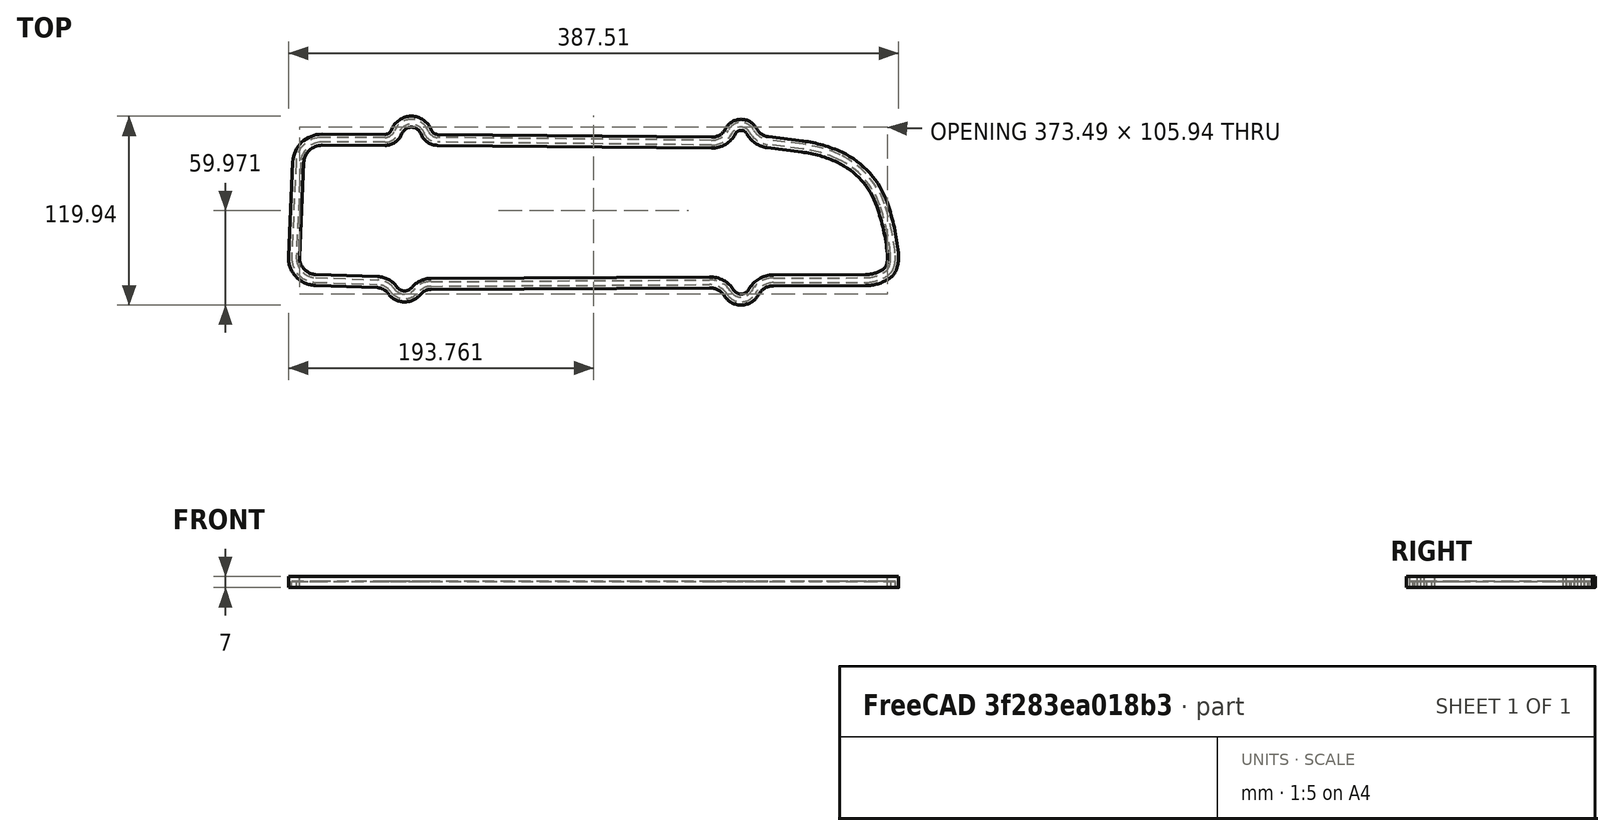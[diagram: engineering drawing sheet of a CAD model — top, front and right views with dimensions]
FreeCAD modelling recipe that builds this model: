
FCSTD DOCUMENT  (FreeCAD 1.1R40971 (Git))
Label: TailLightHousing
License: All rights reserved
LicenseURL: http://en.wikipedia.org/wiki/All_rights_reserved
objects: Sketcher::SketchObject×2, Mesh::Feature×1, PartDesign::Plane×1, App::Point×1, PartDesign::AdditivePipe×1, PartDesign::Body×1
note: 9 computed .brp shape members not serialized (recipe doc carries the construction recipe); baked Part::Feature solids carry a one-line shape summary decoded from their .brp

FEATURE [Mesh::Feature] MeshingTaillightAligned
FEATURE [Sketcher::SketchObject] Sketch  label="GasketPath"
  ArcFitTolerance = 1e-06
  AttachmentSupport = -> [XY_Plane]
  ExternalTypes = [0]
  FullyConstrained = true
  MakeInternals = false
  MapMode = 5
  sketch-geometry (27):
    g0: LineSegment StartX=-100 StartY=-72 StartZ=0 EndX=77 EndY=-71 EndZ=0
    g1: LineSegment StartX=117.5 StartY=-69.75 StartZ=0 EndX=176.08 EndY=-69.5756 EndZ=0
    g2: LineSegment StartX=78.1945 StartY=17.6877 StartZ=0 EndX=-95.75 EndY=19.5 EndZ=0
    g3: LineSegment StartX=-129.25 StartY=19.5 StartZ=0 EndX=-169.243 EndY=19.5618 EndZ=0
    g4: LineSegment StartX=-184.25 StartY=5.25 StartZ=0 EndX=-187 EndY=-54.6239 EndZ=0
    g5: LineSegment StartX=-173.262 StartY=-69.5191 StartZ=0 EndX=-134 EndY=-70.89 EndZ=0
    g6: ArcOfCircle CenterX=-134.428 CenterY=-83.1489 CenterZ=0 NormalX=0 NormalY=0 NormalZ=1 AngleXU=0 Radius=12.2664 StartAngle=0.622932 EndAngle=1.53589
    g7: ArcOfCircle CenterX=-116.75 CenterY=-70.45 CenterZ=0 NormalX=0 NormalY=0 NormalZ=1 AngleXU=0 Radius=9.5 StartAngle=3.76452 EndAngle=5.5955
    g8: ArcOfCircle CenterX=-99.9307 CenterY=-84.2662 CenterZ=0 NormalX=0 NormalY=0 NormalZ=1 AngleXU=0 Radius=12.2664 StartAngle=1.57645 EndAngle=2.45391
    g9: ArcOfCircle CenterX=-172.765 CenterY=-55.2777 CenterZ=0 NormalX=0 NormalY=0 NormalZ=1 AngleXU=0 Radius=14.25 StartAngle=3.0957 EndAngle=4.67749
    g10: ArcOfCircle CenterX=-169.266 CenterY=4.56178 CenterZ=0 NormalX=0 NormalY=0 NormalZ=1 AngleXU=0 Radius=15 StartAngle=1.56925 EndAngle=3.0957
    g11: ArcOfCircle CenterX=-129.238 CenterY=27.5 CenterZ=0 NormalX=0 NormalY=0 NormalZ=1 AngleXU=0 Radius=8 StartAngle=4.71084 EndAngle=5.91373
    g12: ArcOfCircle CenterX=-112.452 CenterY=21 CenterZ=0 NormalX=0 NormalY=0 NormalZ=1 AngleXU=0 Radius=10 StartAngle=0.369433 EndAngle=2.77213
    g13: ArcOfCircle CenterX=-95.6667 CenterY=27.4996 CenterZ=0 NormalX=0 NormalY=0 NormalZ=1 AngleXU=0 Radius=8 StartAngle=3.51103 EndAngle=4.70197
    g14: ArcOfCircle CenterX=77.0819 CenterY=-85.4998 CenterZ=0 NormalX=0 NormalY=0 NormalZ=1 AngleXU=0 Radius=14.5 StartAngle=0.563877 EndAngle=1.57645
    g15: ArcOfCircle CenterX=96.9439 CenterY=-72.9398 CenterZ=0 NormalX=0 NormalY=0 NormalZ=1 AngleXU=0 Radius=9 StartAngle=3.70547 EndAngle=5.78107
    g16: ArcOfCircle CenterX=117.543 CenterY=-84.2499 CenterZ=0 NormalX=0 NormalY=0 NormalZ=1 AngleXU=0 Radius=14.5 StartAngle=1.57377 EndAngle=2.63948
    g17: ArcOfCircle CenterX=78.3352 CenterY=31.187 CenterZ=0 NormalX=0 NormalY=0 NormalZ=1 AngleXU=0 Radius=13.5 StartAngle=4.70197 EndAngle=5.80711
    g18: ArcOfCircle CenterX=97 CenterY=21.5628 CenterZ=0 NormalX=0 NormalY=0 NormalZ=1 AngleXU=0 Radius=7.5 StartAngle=0.494276 EndAngle=2.66552
    g19: ArcOfCircle CenterX=115.707 CenterY=31.6437 CenterZ=0 NormalX=0 NormalY=0 NormalZ=1 AngleXU=0 Radius=13.75 StartAngle=3.63587 EndAngle=4.58795
    g20: LineSegment StartX=114 StartY=18 StartZ=0 EndX=136 EndY=15.2481 EndZ=0
    g21: ArcOfCircle CenterX=126.319 CenterY=-62.1488 CenterZ=0 NormalX=0 NormalY=0 NormalZ=1 AngleXU=0 Radius=78 StartAngle=1.13139 EndAngle=1.44636
    g22: ArcOfCircle CenterX=137.379 CenterY=-38.6186 CenterZ=0 NormalX=0 NormalY=0 NormalZ=1 AngleXU=0 Radius=52 StartAngle=0.329603 EndAngle=1.13139
    g23: ArcOfCircle CenterX=176.009 CenterY=-45.5757 CenterZ=0 NormalX=0 NormalY=0 NormalZ=1 AngleXU=0 Radius=24 StartAngle=4.71537 EndAngle=5.28835
    g24: ArcOfCircle CenterX=184.451 CenterY=-58.5751 CenterZ=0 NormalX=0 NormalY=0 NormalZ=1 AngleXU=0 Radius=8.5 StartAngle=5.28835 EndAngle=5.99521
    g25: ArcOfCircle CenterX=171.986 CenterY=-54.8829 CenterZ=0 NormalX=0 NormalY=0 NormalZ=1 AngleXU=0 Radius=21.5 StartAngle=5.99521 EndAngle=6.38658
    g26: ArcOfCircle CenterX=54.0655 CenterY=-67.1187 CenterZ=0 NormalX=0 NormalY=0 NormalZ=1 AngleXU=0 Radius=140.053 StartAngle=0.103393 EndAngle=0.329603
  constraints (74):
    c: Tangent(g6,g5) = 1.5708
    c: Tangent(g8,g0) = 1.5708
    c: Tangent(g8,g7) = 1.5708
    c: Tangent(g7,g6) = 1.5708
    c: Equal(g6,g8)
    c: DistanceX(g0,g-1) = 100
    c: DistanceY(g0,g-1) = 72
    c: DistanceY(g0,g-1) = 71
    c: Radius(g7) = 9.5
    c: DistanceX(g7,g0) = 16.75
    c: DistanceY(g0,g7) = 1.55
    c: DistanceX(g5,g0) = 34
    c: DistanceY(g0,g5) = 1.11
    c: Tangent(g9,g5) = -1.5708
    c: Tangent(g9,g4) = -1.5708
    c: Radius(g9) = 14.25
    c: DistanceX(g4,g0) = 87
    c: Tangent(g10,g3) = -1.5708
    c: Tangent(g10,g4) = -1.5708
    c: Radius(g10) = 15
    c: DistanceX(g4,g0) = 84.25
    c: DistanceY(g0,g4) = 77.25
    c: Tangent(g11,g3) = 1.5708
    c: Tangent(g12,g11) = 1.5708
    c: Tangent(g13,g12) = 1.5708
    c: Tangent(g13,g2) = 1.5708
    c: Radius(g11) = 8
    c: Radius(g13) = 8
    c: Radius(g12) = 10
    c: DistanceY(g0,g3) = 91.5
    c: DistanceX(g3,g0) = 29.25
    c: DistanceY(g0,g12) = 93
    c: DistanceY(g0,g2) = 91.5
    c: DistanceX(g0,g2) = 4.25
    c: Tangent(g16,g1) = 1.5708
    c: Tangent(g16,g15) = 1.5708
    c: Tangent(g15,g14) = 1.5708
    c: Tangent(g14,g0) = 1.5708
    c: Radius(g15) = 9
    c: Radius(g14) = 14.5
    c: DistanceX(g0,g0) = 177
    c: DistanceY(g14,g0) = 6.75
    c: Radius(g16) = 14.5
    c: DistanceX(g0,g1) = 40.5
    c: DistanceY(g0,g1) = 1.25
    c: Tangent(g20,g19) = -1.5708
    c: Tangent(g19,g18) = 1.5708
    c: Tangent(g18,g17) = 1.5708
    c: Tangent(g17,g2) = 1.5708
    c: Radius(g17) = 13.5
    c: Radius(g18) = 7.5
    c: Radius(g19) = 13.75
    c: DistanceY(g0,g19) = 89
    c: DistanceX(g0,g19) = 37
    c: DistanceX(g0,g18) = 20
    c: DistanceY(g0,g17) = 96
    c: Tangent(g21,g20) = 1.5708
    c: Radius(g21) = 78
    c: Tangent(g22,g21) = -1.5708
    c: Radius(g22) = 52
    c: Tangent(g23,g1) = -1.5708
    c: Radius(g23) = 24
    c: Tangent(g24,g23) = -1.5708
    c: Tangent(g25,g24) = -1.5708
    c: Radius(g24) = 8.5
    c: Radius(g25) = 21.5
    c: Angle(g24) = 0.706858
    c: Tangent(g26,g22) = -1.5708
    c: Tangent(g26,g25) = -1.5708
    c: DistanceX(g1,g23) = 13
    c: DistanceX(g20,g21) = 23.5
    c: DistanceX(g1,g22) = 10.5
    c: DistanceX(g19,g20) = 22
    c: DistanceX(g1,g1) = 58.58
FEATURE [PartDesign::Plane] DatumPlane
  AttachmentSupport = -> [Sketch]
  Length = 110.473
  MapMode = 7
  Placement = pos=(-100,-72,0) rot=(0.579525,-0.57626,-0.57626;2.09114rad)
  ResizeMode = 0
  Width = 63.8978
FEATURE [Sketcher::SketchObject] Sketch001
  ArcFitTolerance = 1e-06
  AttachmentSupport = -> [DatumPlane]
  ExternalTypes = [0]
  FullyConstrained = true
  MakeInternals = false
  MapMode = 5
  Placement = pos=(-100,-72,0) rot=(0.579525,-0.57626,-0.57626;2.09114rad)
  sketch-geometry (8):
    g0: LineSegment StartX=-3.5 StartY=0 StartZ=0 EndX=3.5 EndY=0 EndZ=0
    g1: LineSegment StartX=3.5 StartY=0 StartZ=0 EndX=3.5 EndY=-7 EndZ=0
    g2: LineSegment StartX=-3.5 StartY=-7 StartZ=0 EndX=-3.5 EndY=0 EndZ=0
    g3: LineSegment StartX=-3.5 StartY=-7 StartZ=0 EndX=-1.5 EndY=-7 EndZ=0
    g4: LineSegment StartX=-1.5 StartY=-7 StartZ=0 EndX=-1.5 EndY=-3 EndZ=0
    g5: LineSegment StartX=-1.5 StartY=-3 StartZ=0 EndX=1.5 EndY=-3 EndZ=0
    g6: LineSegment StartX=1.5 StartY=-3 StartZ=0 EndX=1.5 EndY=-7 EndZ=0
    g7: LineSegment StartX=1.5 StartY=-7 StartZ=0 EndX=3.5 EndY=-7 EndZ=0
  constraints (23):
    c: Coincident(g0,g1)
    c: Coincident(g2,g0)
    c: Horizontal(g0)
    c: Vertical(g1)
    c: Vertical(g2)
    c: DistanceY(g1,g1) = -7
    c: Distance(g1,g2) = 7
    c: Symmetric(g0,g0,g-1)
    c: Coincident(g3,g2)
    c: Horizontal(g3)
    c: Coincident(g4,g3)
    c: Vertical(g4)
    c: Coincident(g5,g4)
    c: Horizontal(g5)
    c: Coincident(g6,g5)
    c: Vertical(g6)
    c: Coincident(g7,g6)
    c: Coincident(g7,g1)
    c: Horizontal(g7)
    c: Equal(g3,g7)
    c: DistanceY(g4,g4) = -4
    c: Horizontal(g3,g6)
    c: Distance(g5,g5) = 3
FEATURE [App::Point] Origin001  label="Origin"
  Role = Origin
FEATURE [PartDesign::AdditivePipe] AdditivePipe
  AuxilleryCurvelinear = true
  AuxillerySpineTangent = false
  Binormal = (0,0,0)
  Mode = 0
  Placement = pos=(-100,-72,0) rot=(0.579525,-0.57626,-0.57626;2.09114rad)
  Profile = -> Sketch001
  Refine = true
  Spine = -> Sketch [Edge3,Edge4,Edge5,Edge6,Edge7,Edge8,Edge9,Edge10,Edge11,Edge12,Edge13,Edge14,Edge15,Edge16,Edge17,Edge18,Edge19,Edge20,Edge21,Edge22,Edge23,Edge24,Edge25,Edge26,Edge27,Edge1,Edge2]
  SpineTangent = false
  Suppressed = false
  Transformation = 0
  Transition = 0
FEATURE [PartDesign::Body] Body
  AllowCompound = false
  Group = -> [Sketch,DatumPlane,Sketch001,AdditivePipe]
  Origin = -> Origin
  Tip = -> AdditivePipe
